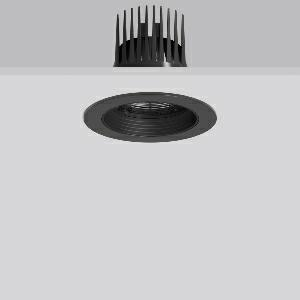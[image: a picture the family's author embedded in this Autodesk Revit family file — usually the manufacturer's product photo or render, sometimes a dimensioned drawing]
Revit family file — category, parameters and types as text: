
# Revit family: heledon_maxi_e_901762_003_3e14
name_source: partatom
category: Lighting Fixtures
units: mm (PartAtom-declared; Revit-internal decimal feet)

## family parameters
Cut with Voids When Loaded = No
Host = Face
Light Source = No
Part Type = Normal
Room Calculation Point = No
Round Connector Dimension = Use Diameter
Shared = No

## types (1)
- HELEDON maxi E (1 x LED Modul 930, 2800 lm, 3000)
    Apparent Load = 25 VA
    Approval mark = CE
    CIE Flux Codes = 96 100 100 100 100
    Color Rendering = 90
    Color Temperature = 3000
    Default Elevation = 1800 mm
    Description = Series: HELEDON maxi
Round recessed downlight. Housing: die-cast aluminium, powder-coated. Black plastic ring and recessed LED to prevent glare from the side. Optical assembly with lens made of plastic (polycarbonate) for the best homogeneous light distribution - can be changed without tools. Best colour rendering index Ra>90. Suitable for Recessed ceiling mounting. Installation without tools thanks to spring fastening system. Including separate LED converter with connecting cable 600 mm.High quality converter without flickering and stroboscopic effect. Through-wiring box (5 pole) available as accessory. The following accessories can be mounted without use of tools: interchangeable lenses, decorative glasses, honeycomb louvre, clear and frosted diffusers, white interchangeable plastic ring. 
Colour: deep black, matt (RAL 9005)
Diameter: 162 mm
Height: 3 mm
Cut-out diameter: 152 mm
Recess height: 200 mm
Luminaire: recess height: 135 mm
Lamp: LED
Socket: without socket
Colour temperature: 3000K
Colour rendering index (CRI): 92
System power: 25 W
Rated luminous flux: 2800 lm
Luminous efficiency: 112 lm/W
Control gear: Regulated power supply
Protection class: II
Type of protection: IP 20
    Height = 0 mm  [stored 0 ft]
    Lamp = 1 x LED Modul 930
    Lamp Light Flux = 2800 lm
    Lamp count = 1
    Length = 162 mm
    Lifetime = 50000 h
    Luminous efficacy = 112 lm/W
    Manufacturer = RZB
    ModVariant = No
    Model = 901762.003
    Mounting Place = Ceiling
    Mounting Type = Recessed
    Number of Poles = 1
    OnlyDefault = Yes
    Power Factor = 1
    Product Name = HELEDON maxi E
    Product group = Recessed downlights
    ProductGroupID = 402
    Protection Class = Protection class II
    Protection Degree = IP 20
    RLX_Detail_Level = 1
    RLX_Emergency_Light_Flux = 0 lm
    RLX_Emergency_Type = 0
    RLX_Emergency_Type_DB = No
    RlxData = <blob elided: 122649 chars, md5=a5bf34b4>
    Socket = socket
    Standby Power = 0 W
    System Light Flux = 2800 lm
    System Power = 25 W
    Type Comments = Product without accessories
    Type Image = 901663.003.jpg
    URL = http://relux.com
    VarID = ---
    Voltage = 230 V
    Voltage Range = 220-240 V
    Weight = 0.00 kg
    Width = 0 mm  [stored 0 ft]

note: [stored X ft] marks values corroborated as IEEE doubles in the binary element streams (Revit-internal decimal feet)

## geometry (parser evidence)
native form markers: Blend x4, Sweep x12
no freeform markers — native parametric forms only
